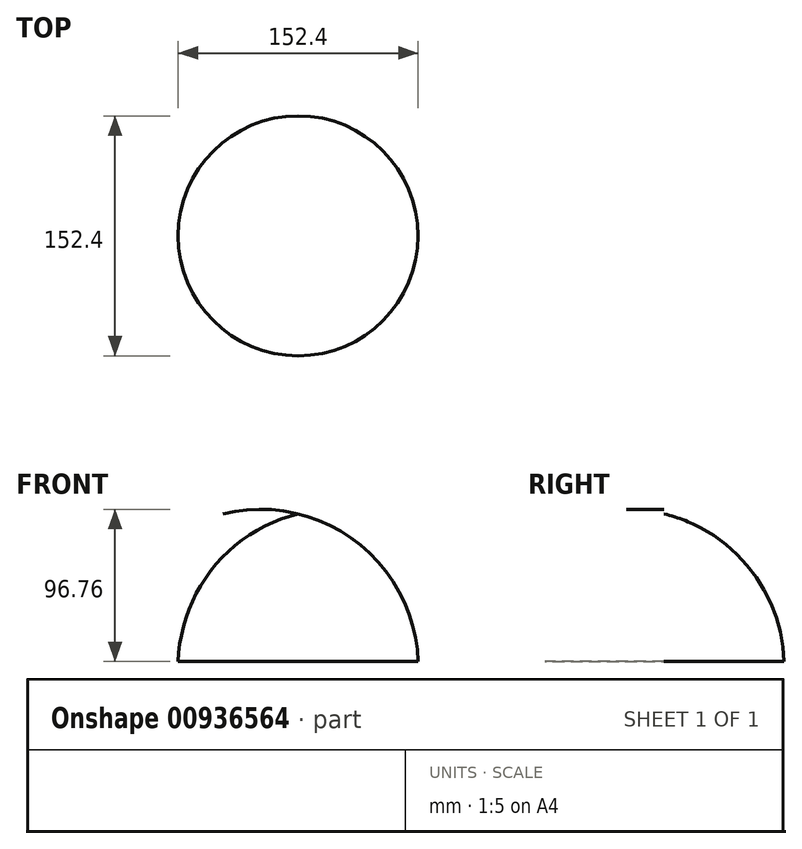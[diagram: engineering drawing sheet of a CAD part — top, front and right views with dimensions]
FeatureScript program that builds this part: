
annotation { "Feature Type Name" : "Feature", "Feature Type Description" : "" }
export const myFeature = defineFeature(function(context is Context, id is Id, definition is map)
    precondition{}
    {
        {
            var Q0;
            Q0=qCreatedBy(makeId("Front.planeOp"),FACE);
            var sketch = newSketch(context, id + "F0", { "sketchPlane" : qUnion([Q0])});
            skArc(sketch, "E0", {"start": v(0, 0) * mm, "mid": v(-53.87, -34.14) * mm, "end": v(-76.2, -93.87) * mm});
            skLineSegment(sketch, "E1", {"start": v(-76.2, -93.87) * mm, "end": v(0, -93.87) * mm});
            skLineSegment(sketch, "E2", {"start": v(0, -93.87) * mm, "end": v(0, 0) * mm});
            skSolve(sketch);
        }
        {
            var Q0;
            Q0 = qSketchRegion(id + "F0", true);
            var Q1;
            Q1=sQuery(id+"F0.wireOp",EDGE,"E2");
            revolve(context, id + "F1", {"surfaceOperationType" : NewSurfaceOperationType.NEW, "entities" : qUnion([Q0]), "axis" : qUnion([Q1]), "revolveType" : RevolveType.FULL});
        }
    });
